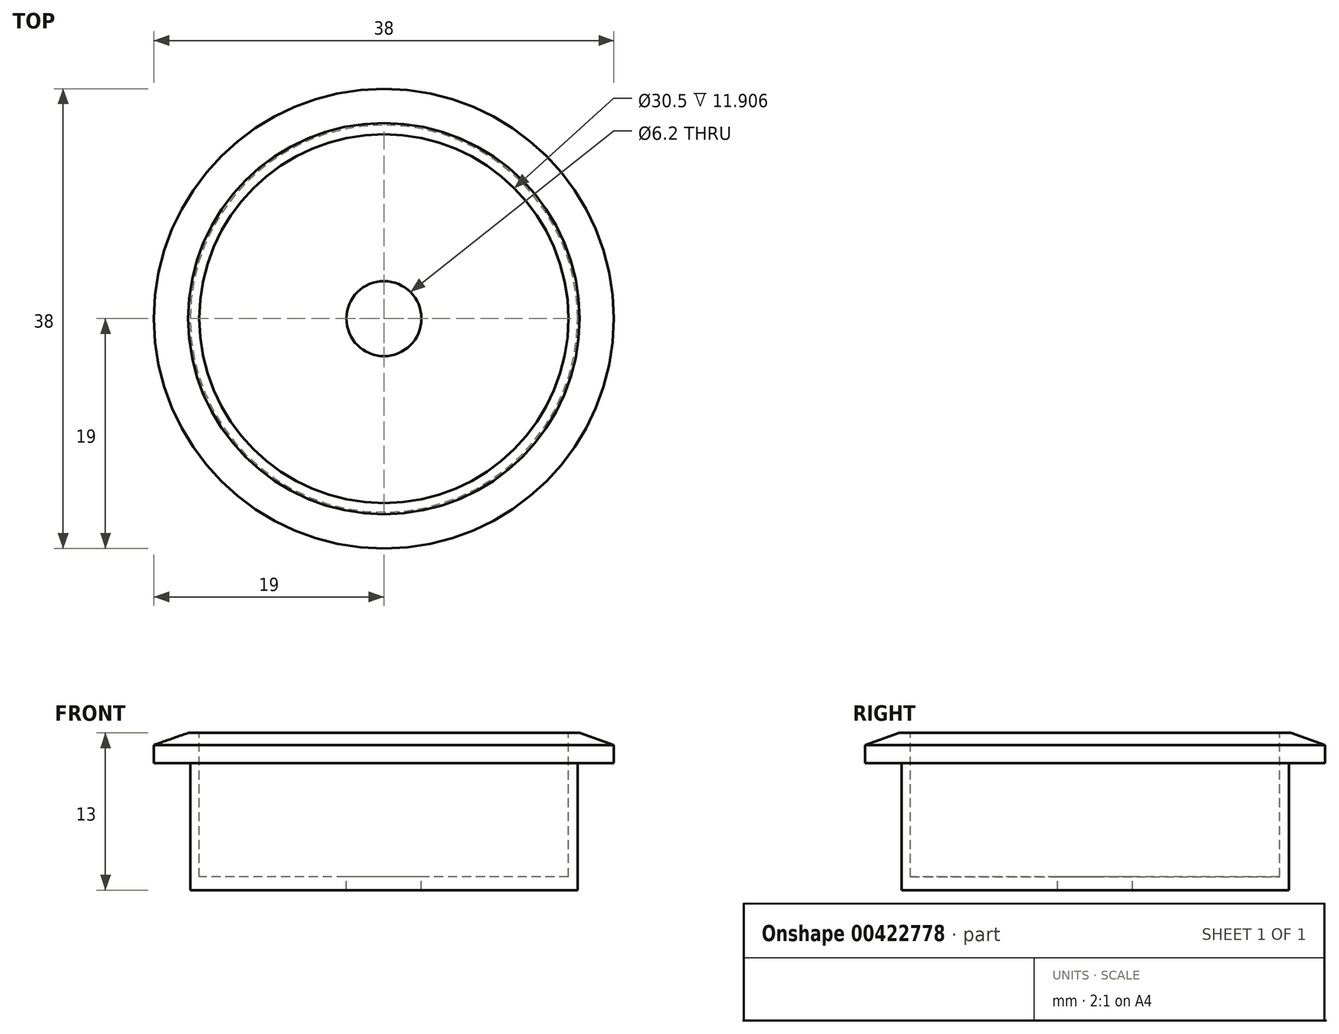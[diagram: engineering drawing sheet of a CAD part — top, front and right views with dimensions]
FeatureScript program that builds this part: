
annotation { "Feature Type Name" : "Feature", "Feature Type Description" : "" }
export const myFeature = defineFeature(function(context is Context, id is Id, definition is map)
    precondition{}
    {
        {
            var Q0;
            Q0=qCreatedBy(makeId("Front.planeOp"),FACE);
            var sketch = newSketch(context, id + "F0", { "sketchPlane" : qUnion([Q0])});
            skLineSegment(sketch, "E0", {"start": v(0, 13) * mm, "end": v(16.17, 13) * mm});
            skLineSegment(sketch, "E1", {"start": v(16.17, 13) * mm, "end": v(19, 12) * mm});
            skLineSegment(sketch, "E2", {"start": v(19, 12) * mm, "end": v(19, 10.5) * mm});
            skLineSegment(sketch, "E3", {"start": v(19, 10.5) * mm, "end": v(16, 10.5) * mm});
            skLineSegment(sketch, "E4", {"start": v(16, 10.5) * mm, "end": v(16, 0) * mm});
            skLineSegment(sketch, "E5", {"start": v(16, 0) * mm, "end": v(0, 0) * mm});
            skLineSegment(sketch, "E6", {"start": v(0, 0) * mm, "end": v(0, 13) * mm});
            skSolve(sketch);
        }
        {
            var Q0;
            Q0=makeQuery(id+"F0.imprint","IMPRINT",FACE,{"disambiguationData":[TD([[makeQuery(id+"F0.imprint","IMPRINT",EDGE,{"derivedFrom":sQuery(id+"F0.wireOp",EDGE,"E0")}),-1.0]])]});
            var Q1;
            Q1=sQuery(id+"F0.wireOp",EDGE,"E6");
            revolve(context, id + "F1", {"entities" : qUnion([Q0]), "axis" : qUnion([Q1]), "revolveType" : RevolveType.FULL});
        }
        {
            var Q0;
            Q0=qCreatedBy(makeId("Front.planeOp"),FACE);
            var sketch = newSketch(context, id + "F2", { "sketchPlane" : qUnion([Q0])});
            skLineSegment(sketch, "E7.bottom", {"start": v(-15.25, 14.1) * mm, "end": v(15.25, 14.1) * mm});
            skLineSegment(sketch, "E7.top", {"start": v(-15.25, 1.1) * mm, "end": v(15.25, 1.1) * mm});
            skLineSegment(sketch, "E7.left", {"start": v(-15.25, 14.1) * mm, "end": v(-15.25, 1.1) * mm});
            skLineSegment(sketch, "E7.right", {"start": v(15.25, 14.1) * mm, "end": v(15.25, 1.1) * mm});
            skLineSegment(sketch, "E8", {"start": v(0, 14.1) * mm, "end": v(0, 1.1) * mm});
            skSolve(sketch);
        }
        {
            var Q0;
            {var subQ0=sQuery(id+"F2.wireOp",EDGE,"E7.right");Q0=makeQuery(id+"F2.imprint","IMPRINT",FACE,{"disambiguationData":[TD([[makeQuery(id+"F2.imprint","IMPRINT",EDGE,{"derivedFrom":subQ0}),-1.0]])]});}
            var Q1;
            Q1=sQuery(id+"F2.wireOp",EDGE,"E8");
            revolve(context, id + "F3", {"entities" : qUnion([Q0]), "axis" : qUnion([Q1]), "revolveType" : RevolveType.FULL});
        }
        {
            var Q0;
            Q0=makeQuery(id+"F3.opRevolve","SWEPT_BODY",BODY,{"disambiguationData":[OSD([sQuery(id+"F2.wireOp",EDGE,"E7.bottom"),sQuery(id+"F2.wireOp",EDGE,"E7.top"),sQuery(id+"F2.wireOp",EDGE,"E7.right"),sQuery(id+"F2.wireOp",EDGE,"E8")])]});
            var Q1;
            Q1=makeQuery(id+"F1.opRevolve","SWEPT_BODY",BODY,{"disambiguationData":[OSD([sQuery(id+"F0.wireOp",EDGE,"E0"),sQuery(id+"F0.wireOp",EDGE,"E1"),sQuery(id+"F0.wireOp",EDGE,"E2"),sQuery(id+"F0.wireOp",EDGE,"E3"),sQuery(id+"F0.wireOp",EDGE,"E4"),sQuery(id+"F0.wireOp",EDGE,"E5"),sQuery(id+"F0.wireOp",EDGE,"E6")])]});
            booleanBodies(context, id + "F4", {"operationType" : BooleanOperationType.SUBTRACTION, "tools" : qUnion([Q0]), "targets" : qUnion([Q1])});
        }
        {
            var Q0;
            Q0=qCreatedBy(makeId("Front.planeOp"),FACE);
            var sketch = newSketch(context, id + "F5", { "sketchPlane" : qUnion([Q0])});
            skLineSegment(sketch, "E9.bottom", {"start": v(0, 3.13) * mm, "end": v(3.1, 3.13) * mm});
            skLineSegment(sketch, "E9.top", {"start": v(0, -1.06) * mm, "end": v(3.1, -1.06) * mm});
            skLineSegment(sketch, "E9.left", {"start": v(0, 3.13) * mm, "end": v(0, -1.06) * mm});
            skLineSegment(sketch, "E9.right", {"start": v(3.1, 3.13) * mm, "end": v(3.1, -1.06) * mm});
            skSolve(sketch);
        }
        {
            var Q0;
            Q0 = qSketchRegion(id + "F5", true);
            var Q1;
            Q1=sQuery(id+"F5.wireOp",EDGE,"E9.left");
            revolve(context, id + "F6", {"entities" : qUnion([Q0]), "axis" : qUnion([Q1]), "revolveType" : RevolveType.FULL});
        }
        {
            var Q0;
            Q0=makeQuery(id+"F6.opRevolve","SWEPT_BODY",BODY,{"disambiguationData":[OSD([sQuery(id+"F5.wireOp",EDGE,"E9.bottom"),sQuery(id+"F5.wireOp",EDGE,"E9.top"),sQuery(id+"F5.wireOp",EDGE,"E9.left"),sQuery(id+"F5.wireOp",EDGE,"E9.right")])]});
            var Q1;
            Q1=makeQuery(id+"F1.opRevolve","SWEPT_BODY",BODY,{"disambiguationData":[OSD([sQuery(id+"F0.wireOp",EDGE,"E0"),sQuery(id+"F0.wireOp",EDGE,"E1"),sQuery(id+"F0.wireOp",EDGE,"E2"),sQuery(id+"F0.wireOp",EDGE,"E3"),sQuery(id+"F0.wireOp",EDGE,"E4"),sQuery(id+"F0.wireOp",EDGE,"E5"),sQuery(id+"F0.wireOp",EDGE,"E6")])]});
            booleanBodies(context, id + "F7", {"operationType" : BooleanOperationType.SUBTRACTION, "tools" : qUnion([Q0]), "targets" : qUnion([Q1])});
        }
    });
